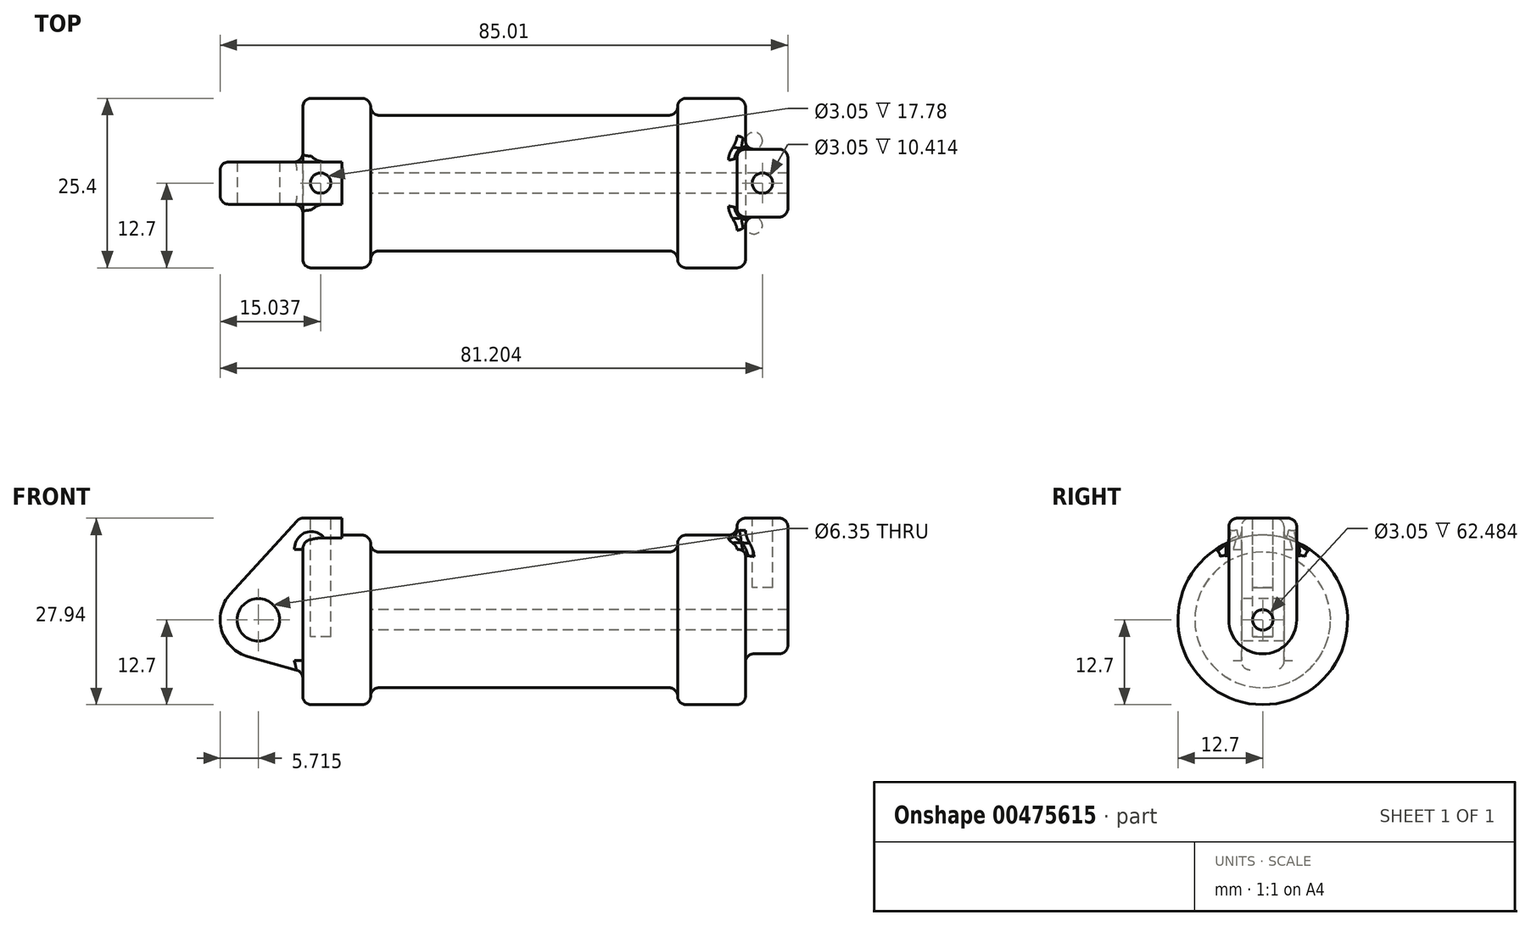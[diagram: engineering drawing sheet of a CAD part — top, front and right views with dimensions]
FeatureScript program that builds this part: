
annotation { "Feature Type Name" : "Feature", "Feature Type Description" : "" }
export const myFeature = defineFeature(function(context is Context, id is Id, definition is map)
    precondition{}
    {
        {
            var Q0;
            Q0=qCreatedBy(makeId("Front.planeOp"),FACE);
            var sketch = newSketch(context, id + "F0", { "sketchPlane" : qUnion([Q0])});
            skLineSegment(sketch, "E0", {"start": v(0, 0) * mm, "end": v(0, 12.7) * mm});
            skLineSegment(sketch, "E1", {"start": v(0, 12.7) * mm, "end": v(10.16, 12.7) * mm});
            skLineSegment(sketch, "E2", {"start": v(10.16, 12.7) * mm, "end": v(10.16, 10.16) * mm});
            skLineSegment(sketch, "E3", {"start": v(10.16, 10.16) * mm, "end": v(56.13, 10.16) * mm});
            skLineSegment(sketch, "E4", {"start": v(56.13, 10.16) * mm, "end": v(56.13, 12.7) * mm});
            skLineSegment(sketch, "E5", {"start": v(56.13, 12.7) * mm, "end": v(66.3, 12.7) * mm});
            skLineSegment(sketch, "E6", {"start": v(66.3, 12.7) * mm, "end": v(66.3, 0) * mm});
            skLineSegment(sketch, "E7", {"start": v(66.3, 0) * mm, "end": v(0, 0) * mm});
            skLineSegment(sketch, "E8", {"start": v(5.84, 15.24) * mm, "end": v(-0.5, 15.24) * mm});
            skLineSegment(sketch, "E9", {"start": v(-0.5, 15.24) * mm, "end": v(-10.88, 3.85) * mm});
            skLineSegment(sketch, "E10", {"start": v(0, 0) * mm, "end": v(-6.65, 0) * mm});
            skCircle(sketch, "E11", {"center": v(-6.65, 0) * mm, "radius": 5.72 * mm});
            skCircle(sketch, "E12", {"center": v(-6.65, 0) * mm, "radius": 3.18 * mm});
            skLineSegment(sketch, "E13", {"start": v(5.84, 15.24) * mm, "end": v(5.84, -9.4) * mm});
            skLineSegment(sketch, "E14", {"start": v(5.84, -9.4) * mm, "end": v(-8.18, -5.5) * mm});
            skSolve(sketch);
        }
        {
            var Q0;
            {var subQ0=sQuery(id+"F0.wireOp",EDGE,"E0");Q0=makeQuery(id+"F0.imprint","IMPRINT",FACE,{"disambiguationData":[TD([[makeQuery(id+"F0.imprint","IMPRINT",EDGE,{"derivedFrom":subQ0}),-1.0]])]});}
            var Q1;
            {var subQ0=sQuery(id+"F0.wireOp",EDGE,"E2");Q1=makeQuery(id+"F0.imprint","IMPRINT",FACE,{"disambiguationData":[TD([[makeQuery(id+"F0.imprint","IMPRINT",EDGE,{"derivedFrom":subQ0}),-1.0]])]});}
            var Q2;
            Q2=sQuery(id+"F0.wireOp",EDGE,"E10");
            revolve(context, id + "F1", {"entities" : qUnion([Q0, Q1]), "axis" : qUnion([Q2]), "revolveType" : RevolveType.FULL});
        }
        {
            var Q0;
            {var subQ0=sQuery(id+"F0.wireOp",EDGE,"E0");Q0=makeQuery(id+"F0.imprint","IMPRINT",FACE,{"disambiguationData":[TD([[makeQuery(id+"F0.imprint","IMPRINT",EDGE,{"derivedFrom":subQ0}),-1.0]])]});}
            var Q1;
            {var subQ1=sQuery(id+"F0.wireOp",EDGE,"E0");Q1=makeQuery(id+"F0.imprint","IMPRINT",FACE,{"disambiguationData":[TD([[makeQuery(id+"F0.imprint","IMPRINT",EDGE,{"derivedFrom":subQ1}),1.0]])]});}
            var Q2;
            {var subQ0=sQuery(id+"F0.wireOp",EDGE,"E14");Q2=makeQuery(id+"F0.imprint","IMPRINT",FACE,{"disambiguationData":[TD([[makeQuery(id+"F0.imprint","IMPRINT",EDGE,{"derivedFrom":subQ0}),-1.0]])]});}
            var Q3;
            {var subQ5=sQuery(id+"F0.wireOp",EDGE,"E12");Q3=makeQuery(id+"F0.imprint","IMPRINT",FACE,{"disambiguationData":[TD([[makeQuery(id+"F0.imprint","IMPRINT",EDGE,{"derivedFrom":subQ5}),-1.0]])]});}
            extrude(context, id + "F2", {"entities" : qUnion([Q0, Q1, Q2, Q3]), "operationType" : NewBodyOperationType.ADD, "endBound" : BoundingType.SYMMETRIC, "oppositeDirection" : true, "depth" : 6.35 * mm});
        }
        {
            var Q0;
            Q0=makeQuery(id+"F1.opRevolve","SWEPT_FACE",FACE,{"disambiguationData":[OSD([sQuery(id+"F0.wireOp",EDGE,"E6")])]});
            var sketch = newSketch(context, id + "F3", { "sketchPlane" : qUnion([Q0])});
            skCircle(sketch, "E15", {"center": v(0, 0) * mm, "radius": 5.08 * mm});
            skCircle(sketch, "E16", {"center": v(0, 0) * mm, "radius": 1.52 * mm});
            skLineSegment(sketch, "E17", {"start": v(-5.08, 0) * mm, "end": v(-5.08, 15.24) * mm});
            skLineSegment(sketch, "E18", {"start": v(-5.08, 15.24) * mm, "end": v(5.08, 15.24) * mm});
            skLineSegment(sketch, "E19", {"start": v(5.08, 15.24) * mm, "end": v(5.08, 0) * mm});
            skSolve(sketch);
        }
        {
            var Q0;
            Q0 = qSketchRegion(id + "F3", true);
            extrude(context, id + "F4", {"entities" : qUnion([Q0]), "operationType" : NewBodyOperationType.ADD, "depth" : 6.35 * mm});
        }
        {
            var Q0;
            Q0 = qSketchRegion(id + "F3", true);
            extrude(context, id + "F5", {"entities" : qUnion([Q0]), "operationType" : NewBodyOperationType.ADD, "oppositeDirection" : true, "depth" : 1.27 * mm});
        }
        {
            var Q0;
            Q0=makeQuery(id+"F3.imprint","IMPRINT",FACE,{"disambiguationData":[TD([[makeQuery(id+"F3.imprint","IMPRINT",EDGE,{"derivedFrom":sQuery(id+"F3.wireOp",EDGE,"E16")}),1.0]])]});
            var Q1;
            Q1=makeQuery(id+"F1.opRevolve","SWEPT_FACE",FACE,{"disambiguationData":[OSD([sQuery(id+"F0.wireOp",EDGE,"E2")])]});
            extrude(context, id + "F6", {"entities" : qUnion([Q0]), "operationType" : NewBodyOperationType.REMOVE, "endBound" : BoundingType.UP_TO_SURFACE, "oppositeDirection" : true, "endBoundEntityFace" : qUnion([Q1]), "depth" : 25.4 * mm});
        }
        {
            var Q0;
            {var subQ0=sQuery(id+"F3.wireOp",EDGE,"E18");Q0=makeQuery(id+"F5.boolean.opBoolean","MERGE",FACE,{"derivedFrom":[makeQuery(id+"F4.opExtrude","SWEPT_FACE",FACE,{"disambiguationData":[OSD([subQ0])]}),makeQuery(id+"F5.opExtrude","SWEPT_FACE",FACE,{"disambiguationData":[OSD([subQ0])]})]});}
            var sketch = newSketch(context, id + "F7", { "sketchPlane" : qUnion([Q0])});
            skLineSegment(sketch, "E20", {"start": v(2.67, 3.18) * mm, "end": v(2.67, -3.18) * mm, "construction": true});
            skLineSegment(sketch, "E21", {"start": v(5.84, 0) * mm, "end": v(-0.5, 0) * mm, "construction": true});
            skCircle(sketch, "E22", {"center": v(2.67, 0) * mm, "radius": 1.52 * mm});
            skLineSegment(sketch, "E23", {"start": v(68.83, 5.08) * mm, "end": v(68.83, -5.08) * mm, "construction": true});
            skLineSegment(sketch, "E24", {"start": v(65.02, 0) * mm, "end": v(72.64, 0) * mm, "construction": true});
            skCircle(sketch, "E25", {"center": v(68.83, 0) * mm, "radius": 1.52 * mm});
            skSolve(sketch);
        }
        {
            var Q0;
            Q0=makeQuery(id+"F7.imprint","IMPRINT",FACE,{"disambiguationData":[TD([[makeQuery(id+"F7.imprint","IMPRINT",EDGE,{"derivedFrom":sQuery(id+"F7.wireOp",EDGE,"E22")}),1.0]])]});
            extrude(context, id + "F8", {"entities" : qUnion([Q0]), "operationType" : NewBodyOperationType.REMOVE, "oppositeDirection" : true, "depth" : 17.78 * mm});
        }
        {
            var Q0;
            Q0=makeQuery(id+"F7.imprint","IMPRINT",FACE,{"disambiguationData":[TD([[makeQuery(id+"F7.imprint","IMPRINT",EDGE,{"derivedFrom":sQuery(id+"F7.wireOp",EDGE,"E25")}),1.0]])]});
            extrude(context, id + "F9", {"entities" : qUnion([Q0]), "operationType" : NewBodyOperationType.REMOVE, "oppositeDirection" : true, "depth" : 10.4 * mm});
        }
        {
            var Q0;
            Q0=makeQuery(id+"F1.opRevolve","SWEPT_FACE",FACE,{"disambiguationData":[OSD([sQuery(id+"F0.wireOp",EDGE,"E0")])]});
            var Q1;
            Q1=makeQuery(id+"F1.opRevolve","SWEPT_FACE",FACE,{"disambiguationData":[OSD([sQuery(id+"F0.wireOp",EDGE,"E4")])]});
            var Q2;
            Q2=makeQuery(id+"F1.opRevolve","SWEPT_FACE",FACE,{"disambiguationData":[OSD([sQuery(id+"F0.wireOp",EDGE,"E2")])]});
            var Q3;
            Q3=makeQuery(id+"F4.boolean.opBoolean","SPLIT",FACE,{"disambiguationData":[TD([makeQuery(id+"F1.opRevolve","SWEPT_FACE",FACE,{"disambiguationData":[OSD([sQuery(id+"F0.wireOp",EDGE,"E5")])]})])],"derivedFrom":makeQuery(id+"F1.opRevolve","SWEPT_FACE",FACE,{"disambiguationData":[OSD([sQuery(id+"F0.wireOp",EDGE,"E6")])]})});
            var Q4;
            Q4=makeQuery(id+"F5.opExtrude","CAP_FACE",FACE,{"disambiguationData":[OSD([sQuery(id+"F3.wireOp",EDGE,"E15"),sQuery(id+"F3.wireOp",EDGE,"E16"),sQuery(id+"F3.wireOp",EDGE,"E17"),sQuery(id+"F3.wireOp",EDGE,"E18"),sQuery(id+"F3.wireOp",EDGE,"E19")])],"isStart":false});
            var Q5;
            {var subQ0=sQuery(id+"F3.wireOp",EDGE,"E19");Q5=makeQuery(id+"F5.boolean.opBoolean","MERGE",FACE,{"derivedFrom":[makeQuery(id+"F4.opExtrude","SWEPT_FACE",FACE,{"disambiguationData":[OSD([subQ0])]}),makeQuery(id+"F5.opExtrude","SWEPT_FACE",FACE,{"disambiguationData":[OSD([subQ0])]})]});}
            var Q6;
            {var subQ0=sQuery(id+"F3.wireOp",EDGE,"E17");Q6=makeQuery(id+"F5.boolean.opBoolean","MERGE",FACE,{"derivedFrom":[makeQuery(id+"F4.opExtrude","SWEPT_FACE",FACE,{"disambiguationData":[OSD([subQ0])]}),makeQuery(id+"F5.opExtrude","SWEPT_FACE",FACE,{"disambiguationData":[OSD([subQ0])]})]});}
            var Q7;
            Q7=makeQuery(id+"F4.opExtrude","CAP_EDGE",EDGE,{"disambiguationData":[OSD([sQuery(id+"F3.wireOp",EDGE,"E18")])],"isStart":false});
            var Q8;
            Q8=makeQuery(id+"F2.opExtrude","CAP_EDGE",EDGE,{"disambiguationData":[OSD([sQuery(id+"F0.wireOp",EDGE,"E8")])],"isStart":false});
            var Q9;
            Q9=makeQuery(id+"F2.opExtrude","CAP_EDGE",EDGE,{"disambiguationData":[OSD([sQuery(id+"F0.wireOp",EDGE,"E8")])],"isStart":true});
            var Q10;
            Q10=makeQuery(id+"F2.opExtrude","SWEPT_FACE",FACE,{"disambiguationData":[OSD([sQuery(id+"F0.wireOp",EDGE,"E9")])]});
            var Q11;
            Q11=makeQuery(id+"F2.opExtrude","SWEPT_FACE",FACE,{"disambiguationData":[OSD([sQuery(id+"F0.wireOp",EDGE,"E14")])]});
            fillet(context, id + "F10", {"entities" : qUnion([Q0, Q1, Q2, Q3, Q4, Q5, Q6, Q7, Q8, Q9, Q10, Q11]), "radius" : 1.27 * mm, "tangentPropagation" : true, "allowEdgeOverflow" : false});
        }
    });
